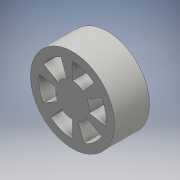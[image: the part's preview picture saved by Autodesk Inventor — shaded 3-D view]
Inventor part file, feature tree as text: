
AUTODESK INVENTOR PART (.ipt)
format: ipt  version: 2016 (Build 200138000, 138)  size: 131,584 bytes
history: native  units: mm
features: extrude x2, sketch x2, pattern_circular x1
ambient origin geometry x8: Origin, YZ Plane, XZ Plane, XY Plane, X Axis, Y Axis, Z Axis, Center Point
bodies: Solid1 (feature_tree)
feature tree (5):
  extrude  "Extrusion1"  Depth=25.0mm TaperAngle=0.0deg
  extrude  "Extrusion2"  Depth=12.0mm
  pattern_circular  "Circular Pattern1"  [2 undecoded]
  sketch  "Sketch1"  dims[d0=60.0mm d1=25.0mm d2=0.0mm]
  sketch  "Sketch2"  dims[d3=6.981317mm d4=12.0mm d5=24.0mm d6=10.0mm d7=0.0mm d8=60.0mm d9=360.0deg]
note: 2 required parameter values undecoded (feature->parameter linkage not recoverable at this tier; creation-order binding heuristic only, values carry confidence <= 0.55)
